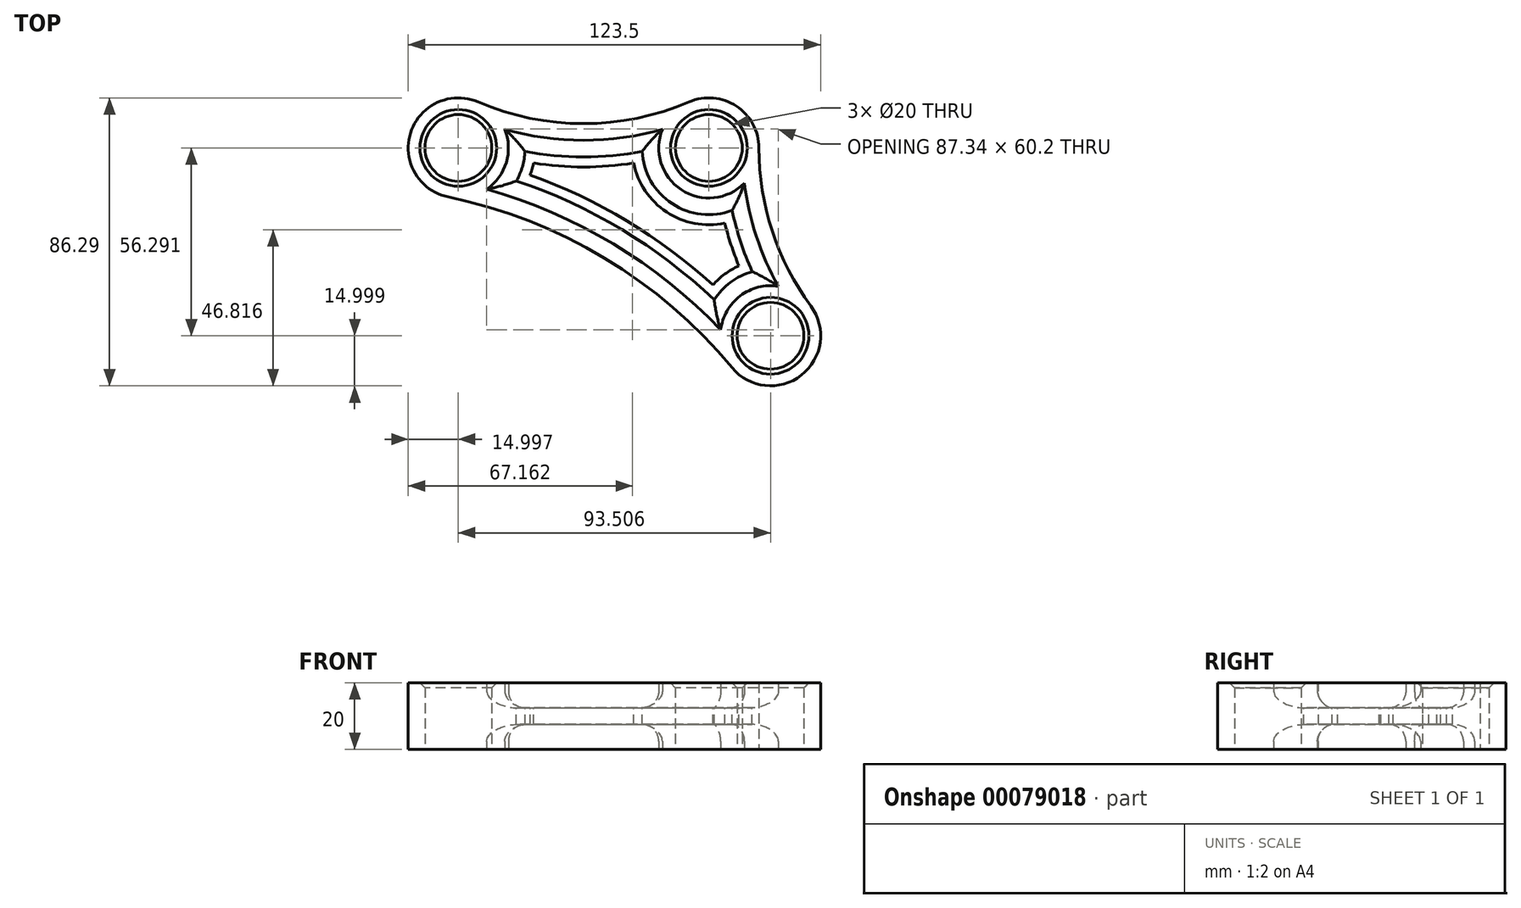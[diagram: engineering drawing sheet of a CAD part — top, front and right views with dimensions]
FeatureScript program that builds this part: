
annotation { "Feature Type Name" : "Feature", "Feature Type Description" : "" }
export const myFeature = defineFeature(function(context is Context, id is Id, definition is map)
    precondition{}
    {
        {
            var Q0;
            Q0=qCreatedBy(makeId("Top.planeOp"),FACE);
            var sketch = newSketch(context, id + "F0", { "sketchPlane" : qUnion([Q0])});
            skCircle(sketch, "E0", {"center": v(0, 0) * mm, "radius": 15 * mm});
            skCircle(sketch, "E1", {"center": v(18.47, -56.3) * mm, "radius": 15 * mm});
            skCircle(sketch, "E2", {"center": v(-75.03, 0) * mm, "radius": 15 * mm});
            skArc(sketch, "E3", {"start": v(-69.1, 13.78) * mm, "mid": v(-37.52, 7.28) * mm, "end": v(-5.92, 13.78) * mm});
            skArc(sketch, "E4", {"start": v(15, 0) * mm, "mid": v(18.99, -24.94) * mm, "end": v(30.56, -47.4) * mm});
            skArc(sketch, "E5", {"start": v(6.92, -65.86) * mm, "mid": v(-31.23, -33.04) * mm, "end": v(-78.08, -14.69) * mm});
            skCircle(sketch, "E6", {"center": v(-75.03, 0) * mm, "radius": 10 * mm});
            skCircle(sketch, "E7", {"center": v(0, 0) * mm, "radius": 10 * mm});
            skCircle(sketch, "E8", {"center": v(18.47, -56.3) * mm, "radius": 10 * mm});
            skArc(sketch, "E9.0", {"start": v(10.77, -62.67) * mm, "mid": v(-28.65, -28.76) * mm, "end": v(-77.07, -9.8) * mm});
            skArc(sketch, "E10.0", {"start": v(-71.08, 9.19) * mm, "mid": v(-37.52, 2.28) * mm, "end": v(-3.95, 9.19) * mm});
            skArc(sketch, "E11.0", {"start": v(10, 0) * mm, "mid": v(14.24, -26.5) * mm, "end": v(26.53, -50.37) * mm});
            skSolve(sketch);
        }
        {
            var Q0;
            {var subQ5=sQuery(id+"F0.wireOp",EDGE,"E2");var subQ8=makeQuery(id+"F0.imprint","INTERSECT",VERTEX,{"derivedFrom":[subQ5,sQuery(id+"F0.wireOp",EDGE,"E3")]});Q0=makeQuery(id+"F0.imprint","IMPRINT",FACE,{"disambiguationData":[TD([[makeQuery(id+"F0.imprint","IMPRINT",EDGE,{"disambiguationData":[TD([[subQ8,1.0]])],"derivedFrom":subQ5}),1.0]])]});}
            var Q1;
            {var subQ0=sQuery(id+"F0.wireOp",EDGE,"E10.0");var subQ1=sQuery(id+"F0.wireOp",EDGE,"E2");var subQ2=makeQuery(id+"F0.imprint","INTERSECT",VERTEX,{"derivedFrom":[subQ1,subQ0]});Q1=makeQuery(id+"F0.imprint","IMPRINT",FACE,{"disambiguationData":[TD([[makeQuery(id+"F0.imprint","IMPRINT",EDGE,{"disambiguationData":[TD([[subQ2,1.0]])],"derivedFrom":subQ1}),1.0]])]});}
            var Q2;
            {var subQ0=sQuery(id+"F0.wireOp",EDGE,"E10.0");var subQ1=sQuery(id+"F0.wireOp",EDGE,"E0");var subQ2=makeQuery(id+"F0.imprint","INTERSECT",VERTEX,{"derivedFrom":[subQ1,subQ0]});Q2=makeQuery(id+"F0.imprint","IMPRINT",FACE,{"disambiguationData":[TD([[makeQuery(id+"F0.imprint","IMPRINT",EDGE,{"disambiguationData":[TD([[subQ2,-1.0]])],"derivedFrom":subQ1}),1.0]])]});}
            var Q3;
            {var subQ5=sQuery(id+"F0.wireOp",EDGE,"E0");var subQ8=makeQuery(id+"F0.imprint","INTERSECT",VERTEX,{"derivedFrom":[subQ5,sQuery(id+"F0.wireOp",EDGE,"E3")]});Q3=makeQuery(id+"F0.imprint","IMPRINT",FACE,{"disambiguationData":[TD([[makeQuery(id+"F0.imprint","IMPRINT",EDGE,{"disambiguationData":[TD([[subQ8,1.0]])],"derivedFrom":subQ5}),1.0]])]});}
            var Q4;
            {var subQ0=sQuery(id+"F0.wireOp",EDGE,"E11.0");var subQ1=sQuery(id+"F0.wireOp",EDGE,"E1");var subQ2=makeQuery(id+"F0.imprint","INTERSECT",VERTEX,{"derivedFrom":[subQ1,subQ0]});Q4=makeQuery(id+"F0.imprint","IMPRINT",FACE,{"disambiguationData":[TD([[makeQuery(id+"F0.imprint","IMPRINT",EDGE,{"disambiguationData":[TD([[subQ2,-1.0]])],"derivedFrom":subQ1}),1.0]])]});}
            var Q5;
            {var subQ5=sQuery(id+"F0.wireOp",EDGE,"E1");var subQ6=makeQuery(id+"F0.imprint","INTERSECT",VERTEX,{"derivedFrom":[subQ5,sQuery(id+"F0.wireOp",EDGE,"E4")]});Q5=makeQuery(id+"F0.imprint","IMPRINT",FACE,{"disambiguationData":[TD([[makeQuery(id+"F0.imprint","IMPRINT",EDGE,{"disambiguationData":[TD([[subQ6,-1.0]])],"derivedFrom":subQ5}),1.0]])]});}
            var Q6;
            {var subQ0=sQuery(id+"F0.wireOp",EDGE,"E5");Q6=makeQuery(id+"F0.imprint","IMPRINT",FACE,{"disambiguationData":[TD([[makeQuery(id+"F0.imprint","IMPRINT",EDGE,{"derivedFrom":subQ0}),-1.0]])]});}
            var Q7;
            {var subQ0=sQuery(id+"F0.wireOp",EDGE,"E3");Q7=makeQuery(id+"F0.imprint","IMPRINT",FACE,{"disambiguationData":[TD([[makeQuery(id+"F0.imprint","IMPRINT",EDGE,{"derivedFrom":subQ0}),-1.0]])]});}
            var Q8;
            {var subQ0=sQuery(id+"F0.wireOp",EDGE,"E4");Q8=makeQuery(id+"F0.imprint","IMPRINT",FACE,{"disambiguationData":[TD([[makeQuery(id+"F0.imprint","IMPRINT",EDGE,{"derivedFrom":subQ0}),-1.0]])]});}
            extrude(context, id + "F1", {"entities" : qUnion([Q0, Q1, Q2, Q3, Q4, Q5, Q6, Q7, Q8]), "endBound" : BoundingType.SYMMETRIC, "depth" : 20 * mm});
        }
        {
            var Q0;
            {var subQ0=sQuery(id+"F0.wireOp",EDGE,"E10.0");var subQ7=sQuery(id+"F0.wireOp",EDGE,"E0");var subQ8=makeQuery(id+"F0.imprint","INTERSECT",VERTEX,{"derivedFrom":[subQ7,subQ0]});Q0=makeQuery(id+"F0.imprint","IMPRINT",FACE,{"disambiguationData":[TD([[makeQuery(id+"F0.imprint","IMPRINT",EDGE,{"disambiguationData":[TD([[subQ8,-1.0]])],"derivedFrom":subQ7}),-1.0]])]});}
            extrude(context, id + "F2", {"entities" : qUnion([Q0]), "operationType" : NewBodyOperationType.ADD, "endBound" : BoundingType.SYMMETRIC, "depth" : 5 * mm});
        }
        {
            var Q0;
            Q0=makeQuery(id+"F2.opExtrude","CAP_FACE",FACE,{"disambiguationData":[OSD([sQuery(id+"F0.wireOp",EDGE,"E0"),sQuery(id+"F0.wireOp",EDGE,"E1"),sQuery(id+"F0.wireOp",EDGE,"E2"),sQuery(id+"F0.wireOp",EDGE,"E9.0"),sQuery(id+"F0.wireOp",EDGE,"E10.0"),sQuery(id+"F0.wireOp",EDGE,"E11.0")])],"isStart":false});
            var Q1;
            Q1=makeQuery(id+"F2.opExtrude","CAP_FACE",FACE,{"disambiguationData":[OSD([sQuery(id+"F0.wireOp",EDGE,"E0"),sQuery(id+"F0.wireOp",EDGE,"E1"),sQuery(id+"F0.wireOp",EDGE,"E2"),sQuery(id+"F0.wireOp",EDGE,"E9.0"),sQuery(id+"F0.wireOp",EDGE,"E10.0"),sQuery(id+"F0.wireOp",EDGE,"E11.0")])],"isStart":true});
            fillet(context, id + "F3", {"entities" : qUnion([Q0, Q1]), "radius" : 5 * mm, "tangentPropagation" : true, "allowEdgeOverflow" : false});
        }
        {
            var Q0;
            Q0=makeQuery(id+"F2.opExtrude","CAP_FACE",FACE,{"disambiguationData":[OSD([sQuery(id+"F0.wireOp",EDGE,"E0"),sQuery(id+"F0.wireOp",EDGE,"E1"),sQuery(id+"F0.wireOp",EDGE,"E2"),sQuery(id+"F0.wireOp",EDGE,"E9.0"),sQuery(id+"F0.wireOp",EDGE,"E10.0"),sQuery(id+"F0.wireOp",EDGE,"E11.0")])],"isStart":false});
            var sketch = newSketch(context, id + "F4", { "sketchPlane" : qUnion([Q0])});
            skArc(sketch, "E12.0", {"start": v(-19.98, -1) * mm, "mid": v(-37.52, -2.72) * mm, "end": v(-55.06, -1) * mm});
            skArc(sketch, "E12.1", {"start": v(-55.06, -1) * mm, "mid": v(-55.83, -5.59) * mm, "end": v(-57.64, -9.88) * mm});
            skArc(sketch, "E12.2", {"start": v(-57.64, -9.88) * mm, "mid": v(-26.07, -24.47) * mm, "end": v(1.6, -45.55) * mm});
            skArc(sketch, "E12.3", {"start": v(6.97, -18.74) * mm, "mid": v(-11, -16.7) * mm, "end": v(-19.98, -1) * mm});
            skArc(sketch, "E12.4", {"start": v(12.98, -37.06) * mm, "mid": v(9.49, -28.06) * mm, "end": v(6.97, -18.74) * mm});
            skArc(sketch, "E12.5", {"start": v(1.6, -45.55) * mm, "mid": v(6.52, -40.26) * mm, "end": v(12.98, -37.06) * mm});
            skArc(sketch, "E13.0", {"start": v(-22.55, -4.51) * mm, "mid": v(-37.52, -5.72) * mm, "end": v(-52.48, -4.51) * mm});
            skArc(sketch, "E13.1", {"start": v(-53.52, -8.14) * mm, "mid": v(-24.52, -21.9) * mm, "end": v(1.21, -41.09) * mm});
            skArc(sketch, "E13.2", {"start": v(1.21, -41.09) * mm, "mid": v(4.8, -37.8) * mm, "end": v(8.98, -35.34) * mm});
            skArc(sketch, "E13.3", {"start": v(-52.48, -4.51) * mm, "mid": v(-52.93, -6.34) * mm, "end": v(-53.52, -8.14) * mm});
            skArc(sketch, "E13.4", {"start": v(8.98, -35.34) * mm, "mid": v(6.64, -29) * mm, "end": v(4.76, -22.5) * mm});
            skArc(sketch, "E13.5", {"start": v(4.76, -22.5) * mm, "mid": v(-12.65, -19.2) * mm, "end": v(-22.55, -4.51) * mm});
            skSolve(sketch);
        }
        {
            var Q0;
            Q0=makeQuery(id+"F4.imprint","IMPRINT",FACE,{"disambiguationData":[TD([[makeQuery(id+"F4.imprint","IMPRINT",EDGE,{"derivedFrom":sQuery(id+"F4.wireOp",EDGE,"E13.0")}),1.0]])]});
            extrude(context, id + "F5", {"entities" : qUnion([Q0]), "operationType" : NewBodyOperationType.REMOVE, "endBound" : BoundingType.THROUGH_ALL, "oppositeDirection" : true, "depth" : 25 * mm});
        }
        {
            var Q0;
            Q0=makeQuery(id+"F1.opExtrude","CAP_EDGE",EDGE,{"disambiguationData":[OSD([sQuery(id+"F0.wireOp",EDGE,"E6")])],"isStart":false});
            var Q1;
            Q1=makeQuery(id+"F1.opExtrude","CAP_EDGE",EDGE,{"disambiguationData":[OSD([sQuery(id+"F0.wireOp",EDGE,"E7")])],"isStart":false});
            var Q2;
            Q2=makeQuery(id+"F1.opExtrude","CAP_EDGE",EDGE,{"disambiguationData":[OSD([sQuery(id+"F0.wireOp",EDGE,"E8")])],"isStart":false});
            chamfer(context, id + "F6", {"entities" : qUnion([Q0, Q1, Q2]), "width" : 1.5 * mm, "tangentPropagation" : true});
        }
    });
